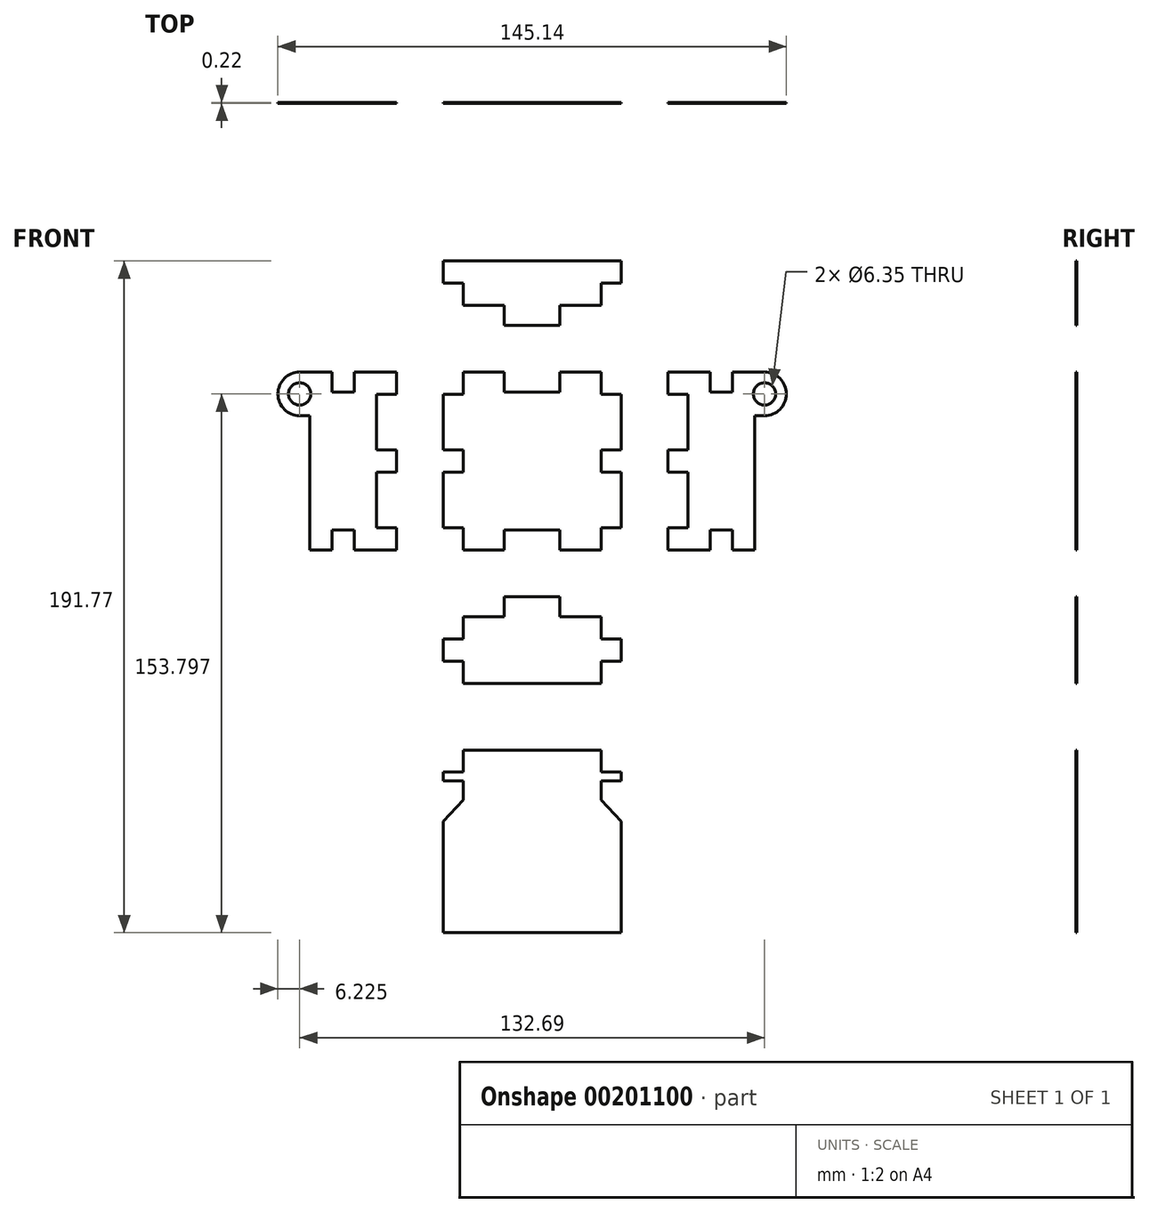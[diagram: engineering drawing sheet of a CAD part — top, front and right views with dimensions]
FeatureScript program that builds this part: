
annotation { "Feature Type Name" : "Feature", "Feature Type Description" : "" }
export const myFeature = defineFeature(function(context is Context, id is Id, definition is map)
    precondition{}
    {
        {
            assignVariable(context, id + "F0", {"name" : "thick", "anyValue" : .224});
        }
        {
            var Q0;
            Q0=qCreatedBy(makeId("Front.planeOp"),FACE);
            var sketch = newSketch(context, id + "F1", { "sketchPlane" : qUnion([Q0])});
            skLineSegment(sketch, "E0.bottom", {"start": v(-25.4, 25.4) * mm, "end": v(25.4, 25.4) * mm});
            skLineSegment(sketch, "E0.top", {"start": v(-25.4, -25.4) * mm, "end": v(25.4, -25.4) * mm});
            skLineSegment(sketch, "E0.left", {"start": v(-25.4, 25.4) * mm, "end": v(-25.4, -25.4) * mm});
            skLineSegment(sketch, "E0.right", {"start": v(25.4, 25.4) * mm, "end": v(25.4, -25.4) * mm});
            skPoint(sketch, "E0.middle", {"position": v(0, 0) * mm});
            skLineSegment(sketch, "E1.bottom", {"start": v(-44.45, 25.4) * mm, "end": v(-63.5, 25.4) * mm});
            skLineSegment(sketch, "E1.top", {"start": v(-44.45, -25.4) * mm, "end": v(-63.5, -25.4) * mm});
            skLineSegment(sketch, "E1.left", {"start": v(-44.45, 25.4) * mm, "end": v(-44.45, -25.4) * mm});
            skLineSegment(sketch, "E1.right", {"start": v(-63.5, 12.95) * mm, "end": v(-63.5, -25.4) * mm});
            skLineSegment(sketch, "E2.bottom", {"start": v(25.4, 44.45) * mm, "end": v(-25.4, 44.45) * mm});
            skLineSegment(sketch, "E2.top", {"start": v(25.4, 57.15) * mm, "end": v(-25.4, 57.15) * mm});
            skLineSegment(sketch, "E2.left", {"start": v(25.4, 44.45) * mm, "end": v(25.4, 57.15) * mm, "construction": true});
            skLineSegment(sketch, "E2.right", {"start": v(-25.4, 44.45) * mm, "end": v(-25.4, 57.15) * mm, "construction": true});
            skCircle(sketch, "E3", {"center": v(-66.34, 19.18) * mm, "radius": 3.18 * mm});
            skArc(sketch, "E4", {"start": v(-66.34, 25.4) * mm, "mid": v(-72.57, 19.18) * mm, "end": v(-66.34, 12.95) * mm});
            skLineSegment(sketch, "E5", {"start": v(-63.5, 25.4) * mm, "end": v(-66.34, 25.4) * mm});
            skLineSegment(sketch, "E6", {"start": v(-66.34, 12.95) * mm, "end": v(-63.5, 12.95) * mm});
            skLineSegment(sketch, "E7", {"start": v(0, 25.4) * mm, "end": v(0, -25.4) * mm, "construction": true});
            skLineSegment(sketch, "E8.MirrorCS", {"start": v(63.5, 25.4) * mm, "end": v(66.34, 25.4) * mm});
            skCircle(sketch, "E9.MirrorC", {"center": v(66.34, 19.18) * mm, "radius": 3.18 * mm});
            skLineSegment(sketch, "E10.MirrorCS", {"start": v(66.34, 12.95) * mm, "end": v(63.5, 12.95) * mm});
            skLineSegment(sketch, "E11.MirrorCS", {"start": v(63.5, 12.95) * mm, "end": v(63.5, -25.4) * mm});
            skLineSegment(sketch, "E12.MirrorCS", {"start": v(44.45, 25.4) * mm, "end": v(44.45, -25.4) * mm});
            skLineSegment(sketch, "E13.MirrorCS", {"start": v(44.45, -25.4) * mm, "end": v(63.5, -25.4) * mm});
            skLineSegment(sketch, "E14.MirrorCS", {"start": v(44.45, 25.4) * mm, "end": v(63.5, 25.4) * mm});
            skArc(sketch, "E15.MirrorCS", {"start": v(66.34, 25.4) * mm, "mid": v(72.57, 19.18) * mm, "end": v(66.34, 12.95) * mm});
            skLineSegment(sketch, "E16.bottom", {"start": v(-25.4, -44.45) * mm, "end": v(25.4, -44.45) * mm});
            skLineSegment(sketch, "E16.top", {"start": v(-25.4, -63.5) * mm, "end": v(25.4, -63.5) * mm});
            skLineSegment(sketch, "E16.left", {"start": v(-25.4, -44.45) * mm, "end": v(-25.4, -63.5) * mm, "construction": true});
            skLineSegment(sketch, "E16.right", {"start": v(25.4, -44.45) * mm, "end": v(25.4, -63.5) * mm, "construction": true});
            skLineSegment(sketch, "E17.bottom", {"start": v(-19.71, -82.55) * mm, "end": v(19.71, -82.55) * mm});
            skLineSegment(sketch, "E17.top", {"start": v(-19.71, -92.71) * mm, "end": v(19.71, -92.71) * mm, "construction": true});
            skLineSegment(sketch, "E17.left", {"start": v(-19.71, -82.55) * mm, "end": v(-19.71, -92.71) * mm});
            skLineSegment(sketch, "E17.right", {"start": v(19.71, -82.55) * mm, "end": v(19.71, -92.71) * mm});
            skLineSegment(sketch, "E18", {"start": v(-19.71, 25.4) * mm, "end": v(-19.71, 19.05) * mm});
            skLineSegment(sketch, "E19", {"start": v(-19.71, 19.05) * mm, "end": v(-25.4, 19.05) * mm});
            skLineSegment(sketch, "E20", {"start": v(-25.4, 3.17) * mm, "end": v(-19.71, 3.17) * mm});
            skLineSegment(sketch, "E21", {"start": v(-19.71, 3.17) * mm, "end": v(-19.71, -3.18) * mm});
            skLineSegment(sketch, "E22", {"start": v(-19.71, -3.18) * mm, "end": v(-25.4, -3.18) * mm});
            skLineSegment(sketch, "E23", {"start": v(-25.4, -19.05) * mm, "end": v(-19.71, -19.05) * mm});
            skLineSegment(sketch, "E24", {"start": v(-19.71, -19.05) * mm, "end": v(-19.71, -25.4) * mm});
            skLineSegment(sketch, "E25", {"start": v(-44.45, 25.4) * mm, "end": v(-38.76, 25.4) * mm});
            skLineSegment(sketch, "E26", {"start": v(-38.76, 25.4) * mm, "end": v(-38.76, 19.05) * mm});
            skLineSegment(sketch, "E27", {"start": v(-38.76, 19.05) * mm, "end": v(-44.45, 19.05) * mm});
            skLineSegment(sketch, "E28", {"start": v(-44.45, 3.17) * mm, "end": v(-38.76, 3.17) * mm});
            skLineSegment(sketch, "E29", {"start": v(-38.76, 3.17) * mm, "end": v(-38.76, -3.18) * mm});
            skLineSegment(sketch, "E30", {"start": v(-38.76, -3.18) * mm, "end": v(-44.45, -3.18) * mm});
            skLineSegment(sketch, "E31", {"start": v(-44.45, -19.05) * mm, "end": v(-38.76, -19.05) * mm});
            skLineSegment(sketch, "E32", {"start": v(-38.76, -19.05) * mm, "end": v(-38.76, -25.4) * mm});
            skLineSegment(sketch, "E33", {"start": v(-38.76, -25.4) * mm, "end": v(-44.45, -25.4) * mm});
            skLineSegment(sketch, "E34.MirrorCS", {"start": v(38.76, 19.05) * mm, "end": v(44.45, 19.05) * mm});
            skLineSegment(sketch, "E35.MirrorCS", {"start": v(38.76, 25.4) * mm, "end": v(38.76, 19.05) * mm});
            skLineSegment(sketch, "E36.MirrorCS", {"start": v(44.45, 3.17) * mm, "end": v(38.76, 3.17) * mm});
            skLineSegment(sketch, "E37.MirrorCS", {"start": v(44.45, 25.4) * mm, "end": v(38.76, 25.4) * mm});
            skLineSegment(sketch, "E38.MirrorCS", {"start": v(38.76, 3.17) * mm, "end": v(38.76, -3.18) * mm});
            skLineSegment(sketch, "E39.MirrorCS", {"start": v(38.76, -3.18) * mm, "end": v(44.45, -3.18) * mm});
            skLineSegment(sketch, "E40.MirrorCS", {"start": v(38.76, -19.05) * mm, "end": v(38.76, -25.4) * mm});
            skLineSegment(sketch, "E41.MirrorCS", {"start": v(38.76, -25.4) * mm, "end": v(44.45, -25.4) * mm});
            skLineSegment(sketch, "E42.MirrorCS", {"start": v(44.45, -19.05) * mm, "end": v(38.76, -19.05) * mm});
            skLineSegment(sketch, "E43.MirrorCS", {"start": v(19.71, 19.05) * mm, "end": v(25.4, 19.05) * mm});
            skLineSegment(sketch, "E44.MirrorCS", {"start": v(19.71, 25.4) * mm, "end": v(19.71, 19.05) * mm});
            skLineSegment(sketch, "E45.MirrorCS", {"start": v(25.4, 3.17) * mm, "end": v(19.71, 3.17) * mm});
            skLineSegment(sketch, "E46.MirrorCS", {"start": v(19.71, 3.17) * mm, "end": v(19.71, -3.18) * mm});
            skLineSegment(sketch, "E47.MirrorCS", {"start": v(19.71, -3.18) * mm, "end": v(25.4, -3.18) * mm});
            skLineSegment(sketch, "E48.MirrorCS", {"start": v(25.4, -19.05) * mm, "end": v(19.71, -19.05) * mm});
            skLineSegment(sketch, "E49.MirrorCS", {"start": v(19.71, -19.05) * mm, "end": v(19.71, -25.4) * mm});
            skLineSegment(sketch, "E50", {"start": v(-7.94, 25.4) * mm, "end": v(-7.94, 19.71) * mm});
            skLineSegment(sketch, "E51", {"start": v(-7.94, 19.71) * mm, "end": v(7.94, 19.71) * mm});
            skLineSegment(sketch, "E52", {"start": v(7.94, 19.71) * mm, "end": v(7.94, 25.4) * mm});
            skPoint(sketch, "E53", {"position": v(0, 19.71) * mm});
            skLineSegment(sketch, "E54", {"start": v(-25.4, 0) * mm, "end": v(25.4, 0) * mm, "construction": true});
            skLineSegment(sketch, "E55.MirrorCS", {"start": v(7.94, -19.71) * mm, "end": v(7.94, -25.4) * mm});
            skLineSegment(sketch, "E56.MirrorCS", {"start": v(-7.94, -19.71) * mm, "end": v(7.94, -19.71) * mm});
            skLineSegment(sketch, "E57.MirrorCS", {"start": v(-7.94, -25.4) * mm, "end": v(-7.94, -19.71) * mm});
            skPoint(sketch, "E58.MirrorP", {"position": v(0, -19.71) * mm});
            skLineSegment(sketch, "E59", {"start": v(-53.97, 25.4) * mm, "end": v(-53.97, 19.71) * mm, "construction": true});
            skLineSegment(sketch, "E60", {"start": v(-53.97, 19.71) * mm, "end": v(-57.15, 19.71) * mm, "construction": true});
            skLineSegment(sketch, "E61", {"start": v(-57.15, 19.71) * mm, "end": v(-57.15, 25.4) * mm});
            skLineSegment(sketch, "E62", {"start": v(-57.15, 19.71) * mm, "end": v(-50.8, 19.71) * mm});
            skLineSegment(sketch, "E63", {"start": v(-50.8, 19.71) * mm, "end": v(-50.8, 25.4) * mm});
            skLineSegment(sketch, "E64", {"start": v(-25.4, 50.8) * mm, "end": v(-31.09, 50.8) * mm, "construction": true});
            skPoint(sketch, "E64.endSnap0", {"position": v(-25.4, 50.8) * mm});
            skLineSegment(sketch, "E65", {"start": v(-31.09, 50.8) * mm, "end": v(-31.09, 57.15) * mm, "construction": true});
            skLineSegment(sketch, "E66", {"start": v(-31.09, 57.15) * mm, "end": v(-25.4, 57.15) * mm, "construction": true});
            skLineSegment(sketch, "E67.MirrorCS", {"start": v(53.97, 19.71) * mm, "end": v(57.15, 19.71) * mm, "construction": true});
            skLineSegment(sketch, "E68.MirrorCS", {"start": v(57.15, 19.71) * mm, "end": v(50.8, 19.71) * mm});
            skLineSegment(sketch, "E69.MirrorCS", {"start": v(57.15, 19.71) * mm, "end": v(57.15, 25.4) * mm});
            skLineSegment(sketch, "E70.MirrorCS", {"start": v(53.97, 25.4) * mm, "end": v(53.97, 19.71) * mm, "construction": true});
            skLineSegment(sketch, "E71.MirrorCS", {"start": v(50.8, 19.71) * mm, "end": v(50.8, 25.4) * mm});
            skPoint(sketch, "E72.MirrorP", {"position": v(25.4, 50.8) * mm});
            skLineSegment(sketch, "E73.MirrorCS", {"start": v(31.09, 57.15) * mm, "end": v(25.4, 57.15) * mm, "construction": true});
            skLineSegment(sketch, "E74.MirrorCS", {"start": v(25.4, 50.8) * mm, "end": v(31.09, 50.8) * mm, "construction": true});
            skLineSegment(sketch, "E75.MirrorCS", {"start": v(31.09, 50.8) * mm, "end": v(31.09, 57.15) * mm, "construction": true});
            skPoint(sketch, "E76.MirrorP", {"position": v(-25.4, -50.8) * mm});
            skLineSegment(sketch, "E77.MirrorCS", {"start": v(-25.4, -50.8) * mm, "end": v(-31.09, -50.8) * mm, "construction": true});
            skLineSegment(sketch, "E78.MirrorCS", {"start": v(-31.09, -57.15) * mm, "end": v(-25.4, -57.15) * mm, "construction": true});
            skLineSegment(sketch, "E79.MirrorCS", {"start": v(-31.09, -50.8) * mm, "end": v(-31.09, -57.15) * mm, "construction": true});
            skPoint(sketch, "E80.MirrorP", {"position": v(25.4, -50.8) * mm});
            skLineSegment(sketch, "E81.MirrorCS", {"start": v(25.4, -50.8) * mm, "end": v(31.09, -50.8) * mm, "construction": true});
            skLineSegment(sketch, "E82.MirrorCS", {"start": v(31.09, -50.8) * mm, "end": v(31.09, -57.15) * mm, "construction": true});
            skLineSegment(sketch, "E83.MirrorCS", {"start": v(31.09, -57.15) * mm, "end": v(25.4, -57.15) * mm, "construction": true});
            skLineSegment(sketch, "E84.MirrorCS", {"start": v(50.8, -19.71) * mm, "end": v(50.8, -25.4) * mm});
            skLineSegment(sketch, "E85.MirrorCS", {"start": v(57.15, -19.71) * mm, "end": v(50.8, -19.71) * mm});
            skLineSegment(sketch, "E86.MirrorCS", {"start": v(57.15, -19.71) * mm, "end": v(57.15, -25.4) * mm});
            skLineSegment(sketch, "E87.MirrorCS", {"start": v(-57.15, -19.71) * mm, "end": v(-57.15, -25.4) * mm});
            skLineSegment(sketch, "E88.MirrorCS", {"start": v(-57.15, -19.71) * mm, "end": v(-50.8, -19.71) * mm});
            skLineSegment(sketch, "E89.MirrorCS", {"start": v(-50.8, -19.71) * mm, "end": v(-50.8, -25.4) * mm});
            skLineSegment(sketch, "E90", {"start": v(-25.4, -102.87) * mm, "end": v(-25.4, -134.62) * mm});
            skLineSegment(sketch, "E91", {"start": v(-25.4, -134.62) * mm, "end": v(25.4, -134.62) * mm});
            skLineSegment(sketch, "E92", {"start": v(25.4, -134.62) * mm, "end": v(25.4, -102.87) * mm});
            skLineSegment(sketch, "E93", {"start": v(-19.71, -88.77) * mm, "end": v(-25.4, -88.77) * mm});
            skLineSegment(sketch, "E94", {"start": v(-25.4, -88.77) * mm, "end": v(-25.4, -91.31) * mm});
            skLineSegment(sketch, "E95", {"start": v(-25.4, -91.31) * mm, "end": v(-19.71, -91.31) * mm});
            skLineSegment(sketch, "E96", {"start": v(-19.71, -92.71) * mm, "end": v(-19.71, -96.77) * mm});
            skLineSegment(sketch, "E97", {"start": v(-19.71, -96.77) * mm, "end": v(-25.4, -102.87) * mm});
            skLineSegment(sketch, "E98.MirrorCS", {"start": v(19.71, -92.71) * mm, "end": v(19.71, -96.77) * mm});
            skLineSegment(sketch, "E99.MirrorCS", {"start": v(19.71, -96.77) * mm, "end": v(25.4, -102.87) * mm});
            skLineSegment(sketch, "E100.MirrorCS", {"start": v(25.4, -88.77) * mm, "end": v(25.4, -91.31) * mm});
            skLineSegment(sketch, "E101.MirrorCS", {"start": v(25.4, -91.31) * mm, "end": v(19.71, -91.31) * mm});
            skLineSegment(sketch, "E102.MirrorCS", {"start": v(19.71, -88.77) * mm, "end": v(25.4, -88.77) * mm});
            skLineSegment(sketch, "E103", {"start": v(-7.94, 44.45) * mm, "end": v(-7.94, 38.76) * mm});
            skLineSegment(sketch, "E104", {"start": v(-7.94, 38.76) * mm, "end": v(7.94, 38.76) * mm});
            skLineSegment(sketch, "E105", {"start": v(7.94, 38.76) * mm, "end": v(7.94, 44.45) * mm});
            skLineSegment(sketch, "E106", {"start": v(-7.94, -44.45) * mm, "end": v(-7.94, -38.76) * mm});
            skLineSegment(sketch, "E107", {"start": v(-7.94, -38.76) * mm, "end": v(7.94, -38.76) * mm});
            skLineSegment(sketch, "E108", {"start": v(7.94, -38.76) * mm, "end": v(7.94, -44.45) * mm});
            skLineSegment(sketch, "E109", {"start": v(-19.71, 44.45) * mm, "end": v(-19.71, 57.15) * mm});
            skLineSegment(sketch, "E110", {"start": v(19.71, 44.45) * mm, "end": v(19.71, 57.15) * mm});
            skLineSegment(sketch, "E111", {"start": v(-19.71, 50.8) * mm, "end": v(-25.4, 50.8) * mm});
            skLineSegment(sketch, "E112", {"start": v(-25.4, 50.8) * mm, "end": v(-25.4, 57.15) * mm});
            skLineSegment(sketch, "E113", {"start": v(25.4, 57.15) * mm, "end": v(25.4, 50.8) * mm});
            skLineSegment(sketch, "E114", {"start": v(19.71, 50.8) * mm, "end": v(25.4, 50.8) * mm});
            skLineSegment(sketch, "E115", {"start": v(-19.71, -44.45) * mm, "end": v(-19.71, -63.5) * mm});
            skLineSegment(sketch, "E116", {"start": v(19.71, -44.45) * mm, "end": v(19.71, -63.5) * mm});
            skLineSegment(sketch, "E117", {"start": v(-19.71, -50.8) * mm, "end": v(-25.4, -50.8) * mm});
            skLineSegment(sketch, "E118", {"start": v(-25.4, -57.15) * mm, "end": v(-25.4, -50.8) * mm});
            skLineSegment(sketch, "E119", {"start": v(-25.4, -57.15) * mm, "end": v(-19.71, -57.15) * mm});
            skLineSegment(sketch, "E120", {"start": v(25.4, -50.8) * mm, "end": v(19.71, -50.8) * mm});
            skLineSegment(sketch, "E121", {"start": v(25.4, -50.8) * mm, "end": v(25.4, -57.15) * mm});
            skLineSegment(sketch, "E122", {"start": v(25.4, -57.15) * mm, "end": v(19.71, -57.15) * mm});
            skPoint(sketch, "E123", {"position": v(25.4, -90.04) * mm});
            skSolve(sketch);
        }
        {
            var Q0;
            {var subQ3=sQuery(id+"F1.wireOp",EDGE,"E2.bottom");Q0=makeQuery(id+"F1.imprint","IMPRINT",FACE,{"disambiguationData":[TD([[makeQuery(id+"F1.imprint","IMPRINT",EDGE,{"derivedFrom":subQ3}),-1.0]])]});}
            var Q1;
            {var subQ2=sQuery(id+"F1.wireOp",EDGE,"E64");Q1=makeQuery(id+"F1.imprint","IMPRINT",FACE,{"disambiguationData":[TD([[makeQuery(id+"F1.imprint","IMPRINT",EDGE,{"derivedFrom":subQ2}),-1.0]])]});}
            var Q2;
            {var subQ0=sQuery(id+"F1.wireOp",EDGE,"E73.MirrorCS");Q2=makeQuery(id+"F1.imprint","IMPRINT",FACE,{"disambiguationData":[TD([[makeQuery(id+"F1.imprint","IMPRINT",EDGE,{"derivedFrom":subQ0}),1.0]])]});}
            var Q3;
            {var subQ0=sQuery(id+"F1.wireOp",EDGE,"E1.right");Q3=makeQuery(id+"F1.imprint","IMPRINT",FACE,{"disambiguationData":[TD([[makeQuery(id+"F1.imprint","IMPRINT",EDGE,{"derivedFrom":subQ0}),1.0]])]});}
            var Q4;
            {var subQ0=sQuery(id+"F1.wireOp",EDGE,"E25");Q4=makeQuery(id+"F1.imprint","IMPRINT",FACE,{"disambiguationData":[TD([[makeQuery(id+"F1.imprint","IMPRINT",EDGE,{"derivedFrom":subQ0}),-1.0]])]});}
            var Q5;
            {var subQ0=sQuery(id+"F1.wireOp",EDGE,"E28");Q5=makeQuery(id+"F1.imprint","IMPRINT",FACE,{"disambiguationData":[TD([[makeQuery(id+"F1.imprint","IMPRINT",EDGE,{"derivedFrom":subQ0}),-1.0]])]});}
            var Q6;
            {var subQ2=sQuery(id+"F1.wireOp",EDGE,"E31");Q6=makeQuery(id+"F1.imprint","IMPRINT",FACE,{"disambiguationData":[TD([[makeQuery(id+"F1.imprint","IMPRINT",EDGE,{"derivedFrom":subQ2}),-1.0]])]});}
            var Q7;
            {var subQ18=sQuery(id+"F1.wireOp",EDGE,"E18");Q7=makeQuery(id+"F1.imprint","IMPRINT",FACE,{"disambiguationData":[TD([[makeQuery(id+"F1.imprint","IMPRINT",EDGE,{"derivedFrom":subQ18}),1.0]])]});}
            var Q8;
            {var subQ6=sQuery(id+"F1.wireOp",EDGE,"E8.MirrorCS");Q8=makeQuery(id+"F1.imprint","IMPRINT",FACE,{"disambiguationData":[TD([[makeQuery(id+"F1.imprint","IMPRINT",EDGE,{"derivedFrom":subQ6}),-1.0]])]});}
            var Q9;
            {var subQ2=sQuery(id+"F1.wireOp",EDGE,"E34.MirrorCS");Q9=makeQuery(id+"F1.imprint","IMPRINT",FACE,{"disambiguationData":[TD([[makeQuery(id+"F1.imprint","IMPRINT",EDGE,{"derivedFrom":subQ2}),1.0]])]});}
            var Q10;
            {var subQ0=sQuery(id+"F1.wireOp",EDGE,"E36.MirrorCS");Q10=makeQuery(id+"F1.imprint","IMPRINT",FACE,{"disambiguationData":[TD([[makeQuery(id+"F1.imprint","IMPRINT",EDGE,{"derivedFrom":subQ0}),1.0]])]});}
            var Q11;
            Q11=makeQuery(id+"F1.imprint","IMPRINT",FACE,{"disambiguationData":[TD([[makeQuery(id+"F1.imprint","IMPRINT",EDGE,{"derivedFrom":sQuery(id+"F1.wireOp",EDGE,"E40.MirrorCS")}),1.0]])]});
            var Q12;
            {var subQ0=sQuery(id+"F1.wireOp",EDGE,"E77.MirrorCS");Q12=makeQuery(id+"F1.imprint","IMPRINT",FACE,{"disambiguationData":[TD([[makeQuery(id+"F1.imprint","IMPRINT",EDGE,{"derivedFrom":subQ0}),1.0]])]});}
            var Q13;
            {var subQ3=sQuery(id+"F1.wireOp",EDGE,"E16.bottom");Q13=makeQuery(id+"F1.imprint","IMPRINT",FACE,{"disambiguationData":[TD([[makeQuery(id+"F1.imprint","IMPRINT",EDGE,{"derivedFrom":subQ3}),-1.0]])]});}
            var Q14;
            {var subQ0=sQuery(id+"F1.wireOp",EDGE,"E81.MirrorCS");Q14=makeQuery(id+"F1.imprint","IMPRINT",FACE,{"disambiguationData":[TD([[makeQuery(id+"F1.imprint","IMPRINT",EDGE,{"derivedFrom":subQ0}),-1.0]])]});}
            var Q15;
            {var subQ7=sQuery(id+"F1.wireOp",EDGE,"E17.bottom");Q15=makeQuery(id+"F1.imprint","IMPRINT",FACE,{"disambiguationData":[TD([[makeQuery(id+"F1.imprint","IMPRINT",EDGE,{"derivedFrom":subQ7}),-1.0]])]});}
            var Q16;
            {var subQ0=sQuery(id+"F1.wireOp",EDGE,"E93");Q16=makeQuery(id+"F1.imprint","IMPRINT",FACE,{"disambiguationData":[TD([[makeQuery(id+"F1.imprint","IMPRINT",EDGE,{"derivedFrom":subQ0}),1.0]])]});}
            var Q17;
            Q17=makeQuery(id+"F1.imprint","IMPRINT",FACE,{"disambiguationData":[TD([[makeQuery(id+"F1.imprint","IMPRINT",EDGE,{"derivedFrom":sQuery(id+"F1.wireOp",EDGE,"E100.MirrorCS")}),-1.0]])]});
            var Q18;
            {var subQ0=sQuery(id+"F1.wireOp",EDGE,"E103");Q18=makeQuery(id+"F1.imprint","IMPRINT",FACE,{"disambiguationData":[TD([[makeQuery(id+"F1.imprint","IMPRINT",EDGE,{"derivedFrom":subQ0}),1.0]])]});}
            var Q19;
            {var subQ0=sQuery(id+"F1.wireOp",EDGE,"E106");Q19=makeQuery(id+"F1.imprint","IMPRINT",FACE,{"disambiguationData":[TD([[makeQuery(id+"F1.imprint","IMPRINT",EDGE,{"derivedFrom":subQ0}),-1.0]])]});}
            var Q20;
            {var subQ0=sQuery(id+"F1.wireOp",EDGE,"E117");Q20=makeQuery(id+"F1.imprint","IMPRINT",FACE,{"disambiguationData":[TD([[makeQuery(id+"F1.imprint","IMPRINT",EDGE,{"derivedFrom":subQ0}),1.0]])]});}
            var Q21;
            {var subQ0=sQuery(id+"F1.wireOp",EDGE,"E120");Q21=makeQuery(id+"F1.imprint","IMPRINT",FACE,{"disambiguationData":[TD([[makeQuery(id+"F1.imprint","IMPRINT",EDGE,{"derivedFrom":subQ0}),1.0]])]});}
            var Q22;
            {var subQ4=sQuery(id+"F1.wireOp",EDGE,"E111");Q22=makeQuery(id+"F1.imprint","IMPRINT",FACE,{"disambiguationData":[TD([[makeQuery(id+"F1.imprint","IMPRINT",EDGE,{"derivedFrom":subQ4}),-1.0]])]});}
            var Q23;
            {var subQ0=sQuery(id+"F1.wireOp",EDGE,"E113");Q23=makeQuery(id+"F1.imprint","IMPRINT",FACE,{"disambiguationData":[TD([[makeQuery(id+"F1.imprint","IMPRINT",EDGE,{"derivedFrom":subQ0}),-1.0]])]});}
            extrude(context, id + "F2", {"entities" : qUnion([Q0, Q1, Q2, Q3, Q4, Q5, Q6, Q7, Q8, Q9, Q10, Q11, Q12, Q13, Q14, Q15, Q16, Q17, Q18, Q19, Q20, Q21, Q22, Q23]), "depth" : (getVariable(context, 'thick')) * mm});
        }
    });
